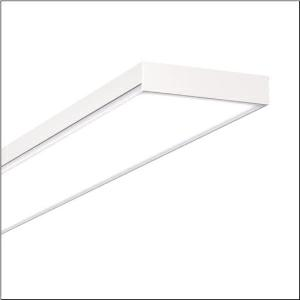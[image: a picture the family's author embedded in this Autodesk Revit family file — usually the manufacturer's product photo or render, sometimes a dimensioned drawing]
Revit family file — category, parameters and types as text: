
# Revit family: apollon_r__31_surface_51mp25wm2441wa_3dc9
name_source: partatom
category: Lighting Fixtures
units: mm (PartAtom-declared; Revit-internal decimal feet)

## family parameters
Cut with Voids When Loaded = No
Host = Face
Light Source = No
Part Type = Normal
Room Calculation Point = No
Round Connector Dimension = Use Diameter
Shared = No

## types (1)
- Apollon® 31 Surface (1 x LED, 3800 lm, 27 W, 4000K)
    Apparent Load = 27 VA
    CIE Flux Codes = 61 87 97 97 100
    Color Rendering = 80
    Color Temperature = 4000K
    Default Elevation = 1800 mm
    Description = Apollon® 31 Surface, office luminaire, primary optical cover: micro prismatic cover, of PMMA, light emission: direct distribution, primary light characteristic: symmetric, installation type: surface-mounted, LED, rated luminous flux: 3.800lm, luminous efficacy: 139lm/W, light colour: 840, colour temperature: 4000K, control gear: ECG Multilumen, with terminal, 3-pole, mains connection: 220..240V, AC, 50/60Hz, rated input power: 27W, housing, of sheet steel, coil coated, traffic white (RAL 9016), length: 1.245mm, width: 200mm, height: 44mm, protection rating (complete): IP20, insulation class (complete): insulation class II (safety insulation), certification: CE, impact resistance: IK02, permissible operating ambient temperature: -20..+40°C, packaging unit: 1 piece
    Height = 44 mm
    Lamp = 1 x LED
    Lamp Light Flux = 3800 lm
    Lamp Power = 27 W
    Lamp count = 1
    Length = 1245 mm
    Luminous efficacy = 141 lm/W
    Manufacturer = Siteco
    ModVariant = No
    Model = 51MP25WM2441WA
    Mounting Place = Ceiling
    Mounting Type = Surface mounted
    Number of Poles = 1
    OnlyDefault = Yes
    Power Factor = 1
    Product Name = Apollon® 31 Surface
    Product group = office luminaire | ceiling mounted
    ProductGroupID = 300
    Protection Class = Protection class II
    Protection Degree = IP 20
    RLX_Detail_Level = 1
    RLX_Emergency_Light_Flux = 0 lm
    RLX_Emergency_Type = 0
    RLX_Emergency_Type_DB = No
    RlxData = <blob elided: 20721 chars, md5=656da554>
    Socket = socket
    Standby Power = 0 W
    System Light Flux = 3800 lm
    System Power = 27 W
    Type Comments = Product without accessories
    Type Image = l_1313658.jpg
    URL = http://relux.com
    VarID = ---
    Voltage = 0 V
    Weight = 0.00 kg
    Width = 200 mm  [stored 0.656168 ft]

note: [stored X ft] marks values corroborated as IEEE doubles in the binary element streams (Revit-internal decimal feet)

## geometry (parser evidence)
native form markers: Blend x4, Sweep x13
no freeform markers — native parametric forms only
